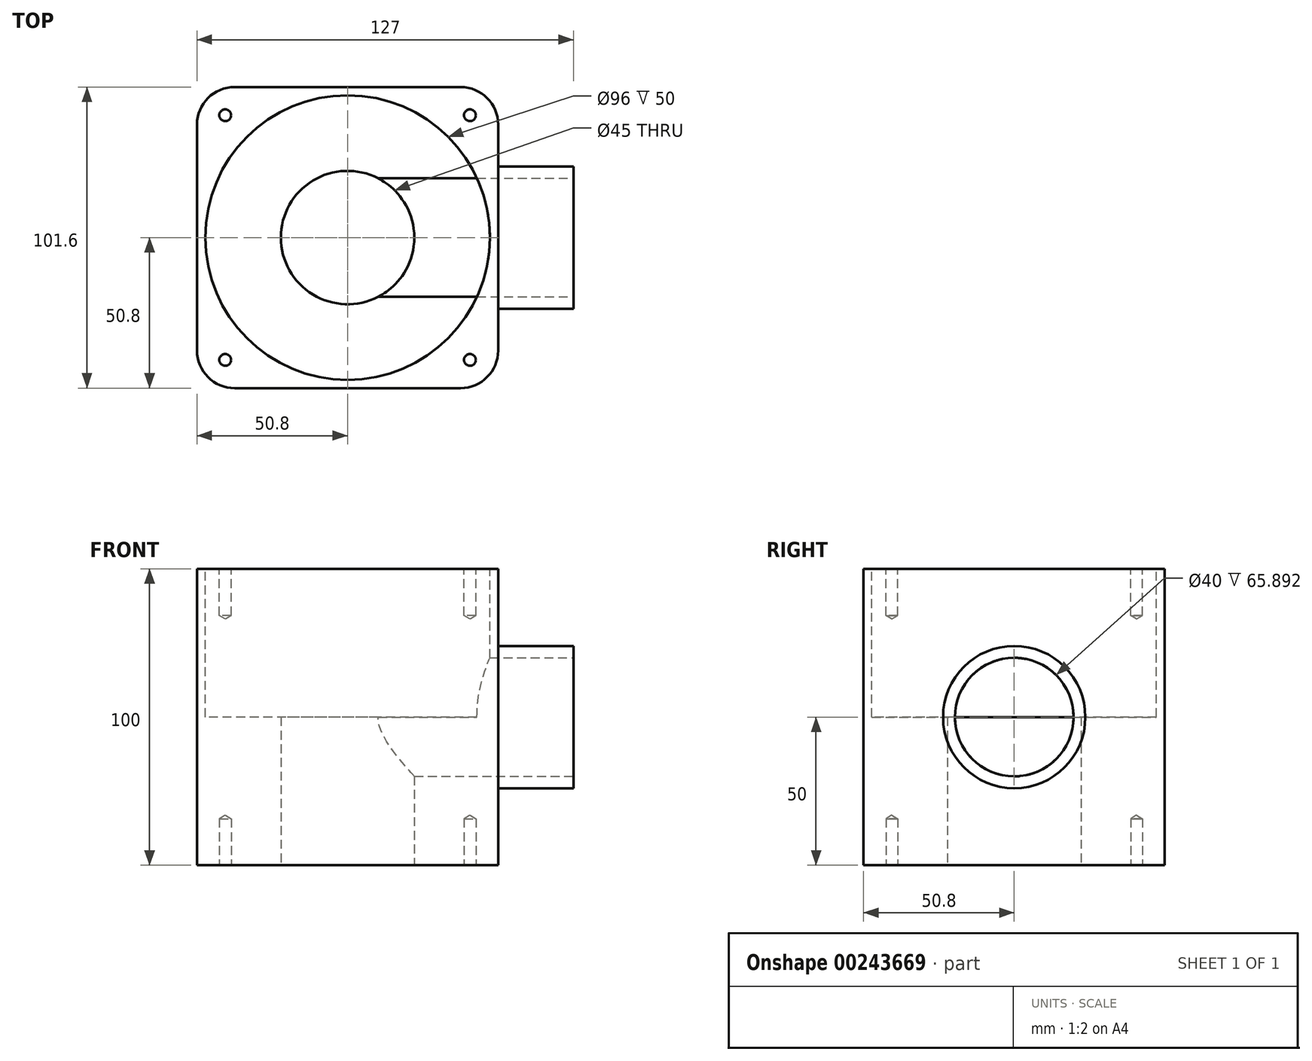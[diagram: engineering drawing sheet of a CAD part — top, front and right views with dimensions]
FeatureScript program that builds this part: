
annotation { "Feature Type Name" : "Feature", "Feature Type Description" : "" }
export const myFeature = defineFeature(function(context is Context, id is Id, definition is map)
    precondition{}
    {
        {
            var Q0;
            Q0=qCreatedBy(makeId("Top.planeOp"),FACE);
            var sketch = newSketch(context, id + "F0", { "sketchPlane" : qUnion([Q0])});
            skLineSegment(sketch, "E0.bottom", {"start": v(-50.8, -50.8) * mm, "end": v(50.8, -50.8) * mm});
            skLineSegment(sketch, "E0.top", {"start": v(-50.8, 50.8) * mm, "end": v(50.8, 50.8) * mm});
            skLineSegment(sketch, "E0.left", {"start": v(-50.8, -50.8) * mm, "end": v(-50.8, 50.8) * mm});
            skLineSegment(sketch, "E0.right", {"start": v(50.8, -50.8) * mm, "end": v(50.8, 50.8) * mm});
            skPoint(sketch, "E0.middle", {"position": v(0, 0) * mm});
            skCircle(sketch, "E1", {"center": v(0, 0) * mm, "radius": 48 * mm});
            skSolve(sketch);
        }
        {
            var Q0;
            Q0 = qSketchRegion(id + "F0", true);
            var Q1;
            Q1=makeQuery(id+"F0.imprint","IMPRINT",FACE,{"disambiguationData":[TD([[makeQuery(id+"F0.imprint","IMPRINT",EDGE,{"derivedFrom":sQuery(id+"F0.wireOp",EDGE,"E1")}),1.0]])]});
            extrude(context, id + "F1", {"entities" : qUnion([Q0, Q1]), "endBound" : BoundingType.SYMMETRIC, "depth" : 100 * mm});
        }
        {
            var Q0;
            Q0=makeQuery(id+"F1.opExtrude","SWEPT_FACE",FACE,{"disambiguationData":[OSD([sQuery(id+"F0.wireOp",EDGE,"E0.right")])]});
            var sketch = newSketch(context, id + "F2", { "sketchPlane" : qUnion([Q0])});
            skCircle(sketch, "E2", {"center": v(0, 0) * mm, "radius": 20 * mm});
            skSolve(sketch);
        }
        {
            var Q0;
            Q0 = qSketchRegion(id + "F2", true);
            extrude(context, id + "F3", {"entities" : qUnion([Q0]), "operationType" : NewBodyOperationType.REMOVE, "oppositeDirection" : true, "depth" : 50.8 * mm});
        }
        {
            var Q0;
            Q0=makeQuery(id+"F1.opExtrude","CAP_FACE",FACE,{"disambiguationData":[OSD([sQuery(id+"F0.wireOp",EDGE,"E0.bottom"),sQuery(id+"F0.wireOp",EDGE,"E0.top"),sQuery(id+"F0.wireOp",EDGE,"E0.left"),sQuery(id+"F0.wireOp",EDGE,"E0.right")])],"isStart":false});
            var sketch = newSketch(context, id + "F4", { "sketchPlane" : qUnion([Q0])});
            skCircle(sketch, "E3", {"center": v(0, 0) * mm, "radius": 48 * mm});
            skSolve(sketch);
        }
        {
            var Q0;
            Q0=makeQuery(id+"F4.imprint","IMPRINT",FACE,{"disambiguationData":[TD([[makeQuery(id+"F4.imprint","IMPRINT",EDGE,{"derivedFrom":sQuery(id+"F4.wireOp",EDGE,"E3")}),1.0]])]});
            extrude(context, id + "F5", {"entities" : qUnion([Q0]), "operationType" : NewBodyOperationType.REMOVE, "oppositeDirection" : true, "depth" : 50 * mm});
        }
        {
            var Q0;
            Q0=makeQuery(id+"F1.opExtrude","CAP_FACE",FACE,{"disambiguationData":[OSD([sQuery(id+"F0.wireOp",EDGE,"E0.bottom"),sQuery(id+"F0.wireOp",EDGE,"E0.top"),sQuery(id+"F0.wireOp",EDGE,"E0.left"),sQuery(id+"F0.wireOp",EDGE,"E0.right")])],"isStart":true});
            var sketch = newSketch(context, id + "F6", { "sketchPlane" : qUnion([Q0])});
            skCircle(sketch, "E4", {"center": v(0, 0) * mm, "radius": 22.5 * mm});
            skSolve(sketch);
        }
        {
            var Q0;
            Q0 = qSketchRegion(id + "F6", true);
            extrude(context, id + "F7", {"entities" : qUnion([Q0]), "operationType" : NewBodyOperationType.REMOVE, "endBound" : BoundingType.THROUGH_ALL, "oppositeDirection" : true, "depth" : 25.4 * mm});
        }
        {
            var Q0;
            Q0=makeQuery(id+"F1.opExtrude","SWEPT_FACE",FACE,{"disambiguationData":[OSD([sQuery(id+"F0.wireOp",EDGE,"E0.right")])]});
            var sketch = newSketch(context, id + "F8", { "sketchPlane" : qUnion([Q0])});
            skCircle(sketch, "E5", {"center": v(0, 0) * mm, "radius": 24 * mm});
            skCircle(sketch, "E6.0", {"center": v(0, 0) * mm, "radius": 20 * mm});
            skSolve(sketch);
        }
        {
            var Q0;
            Q0 = qSketchRegion(id + "F8", true);
            extrude(context, id + "F9", {"entities" : qUnion([Q0]), "operationType" : NewBodyOperationType.ADD, "depth" : 25.4 * mm});
        }
        {
            var Q0;
            Q0=makeQuery(id+"F1.opExtrude","SWEPT_EDGE",EDGE,{"disambiguationData":[OSD([sQuery(id+"F0.wireOp",EDGE,"E0.bottom"),sQuery(id+"F0.wireOp",EDGE,"E0.right")])]});
            var Q1;
            Q1=makeQuery(id+"F1.opExtrude","SWEPT_EDGE",EDGE,{"disambiguationData":[OSD([sQuery(id+"F0.wireOp",EDGE,"E0.bottom"),sQuery(id+"F0.wireOp",EDGE,"E0.left")])]});
            var Q2;
            Q2=makeQuery(id+"F1.opExtrude","SWEPT_EDGE",EDGE,{"disambiguationData":[OSD([sQuery(id+"F0.wireOp",EDGE,"E0.top"),sQuery(id+"F0.wireOp",EDGE,"E0.right")])]});
            var Q3;
            Q3=makeQuery(id+"F1.opExtrude","SWEPT_EDGE",EDGE,{"disambiguationData":[OSD([sQuery(id+"F0.wireOp",EDGE,"E0.top"),sQuery(id+"F0.wireOp",EDGE,"E0.left")])]});
            fillet(context, id + "F10", {"entities" : qUnion([Q0, Q1, Q2, Q3]), "radius" : 12.7 * mm, "tangentPropagation" : true, "allowEdgeOverflow" : false});
        }
        {
            var Q0;
            Q0=makeQuery(id+"F1.opExtrude","CAP_FACE",FACE,{"disambiguationData":[OSD([sQuery(id+"F0.wireOp",EDGE,"E0.bottom"),sQuery(id+"F0.wireOp",EDGE,"E0.top"),sQuery(id+"F0.wireOp",EDGE,"E0.left"),sQuery(id+"F0.wireOp",EDGE,"E0.right")])],"isStart":false});
            var sketch = newSketch(context, id + "F11", { "sketchPlane" : qUnion([Q0])});
            skLineSegment(sketch, "E7.bottom", {"start": v(-41.28, -41.28) * mm, "end": v(41.28, -41.28) * mm, "construction": true});
            skLineSegment(sketch, "E7.top", {"start": v(-41.28, 41.28) * mm, "end": v(41.28, 41.28) * mm, "construction": true});
            skLineSegment(sketch, "E7.left", {"start": v(-41.28, -41.28) * mm, "end": v(-41.28, 41.28) * mm, "construction": true});
            skLineSegment(sketch, "E7.right", {"start": v(41.28, -41.27) * mm, "end": v(41.28, 41.28) * mm, "construction": true});
            skPoint(sketch, "E7.middle", {"position": v(0, 0) * mm});
            skSolve(sketch);
        }
        {
            var Q0;
            Q0=sQuery(id+"F11.wireOp",VERTEX,"E7.top.start");
            var Q1;
            Q1=sQuery(id+"F11.wireOp",VERTEX,"E7.top.end");
            var Q2;
            Q2=sQuery(id+"F11.wireOp",VERTEX,"E7.bottom.end");
            var Q3;
            Q3=sQuery(id+"F11.wireOp",VERTEX,"E7.bottom.start");
            var Q4;
            Q4=makeQuery(id+"F1.opExtrude","SWEPT_BODY",BODY,{"disambiguationData":[OSD([sQuery(id+"F0.wireOp",EDGE,"E0.bottom"),sQuery(id+"F0.wireOp",EDGE,"E0.top"),sQuery(id+"F0.wireOp",EDGE,"E0.left"),sQuery(id+"F0.wireOp",EDGE,"E0.right")])]});
            hole(context, id + "F12", {"style" : HoleStyle.SIMPLE, "endStyle" : HoleEndStyle.BLIND, "standardTappedOrClearance" : lookupTablePath({ "standard" : "ISO", "engagement" : "75%", "pitch" : "1 mm", "size" : "M5", "type" : "Tapped" }), "standardBlindInLast" : lookupTablePath({ "standard" : "ISO", "engagement" : "75%", "pitch" : "1 mm", "size" : "M5", "type" : "Tapped" }), "holeDiameter" : 4 * mm, "showTappedDepth" : true, "holeDepth" : 15.7 * mm, "tappedDepth" : 12.7 * mm, "tapClearance" : 3, "locations" : qUnion([Q0, Q1, Q2, Q3]), "scope" : qUnion([Q4])});
        }
        {
            var Q0;
            Q0=makeQuery(id+"F1.opExtrude","CAP_FACE",FACE,{"disambiguationData":[OSD([sQuery(id+"F0.wireOp",EDGE,"E0.bottom"),sQuery(id+"F0.wireOp",EDGE,"E0.top"),sQuery(id+"F0.wireOp",EDGE,"E0.left"),sQuery(id+"F0.wireOp",EDGE,"E0.right")])],"isStart":true});
            var sketch = newSketch(context, id + "F13", { "sketchPlane" : qUnion([Q0])});
            skLineSegment(sketch, "E8.bottom", {"start": v(-41.28, -41.28) * mm, "end": v(41.28, -41.28) * mm, "construction": true});
            skLineSegment(sketch, "E8.top", {"start": v(-41.28, 41.28) * mm, "end": v(41.28, 41.28) * mm, "construction": true});
            skLineSegment(sketch, "E8.left", {"start": v(-41.28, -41.28) * mm, "end": v(-41.28, 41.28) * mm, "construction": true});
            skLineSegment(sketch, "E8.right", {"start": v(41.28, -41.28) * mm, "end": v(41.28, 41.27) * mm, "construction": true});
            skPoint(sketch, "E8.middle", {"position": v(0, 0) * mm});
            skSolve(sketch);
        }
        {
            var Q0;
            Q0=sQuery(id+"F13.wireOp",VERTEX,"E8.left.end");
            var Q1;
            Q1=sQuery(id+"F13.wireOp",VERTEX,"E8.right.end");
            var Q2;
            Q2=sQuery(id+"F13.wireOp",VERTEX,"E8.left.start");
            var Q3;
            Q3=sQuery(id+"F13.wireOp",VERTEX,"E8.right.start");
            var Q4;
            Q4=makeQuery(id+"F1.opExtrude","SWEPT_BODY",BODY,{"disambiguationData":[OSD([sQuery(id+"F0.wireOp",EDGE,"E0.bottom"),sQuery(id+"F0.wireOp",EDGE,"E0.top"),sQuery(id+"F0.wireOp",EDGE,"E0.left"),sQuery(id+"F0.wireOp",EDGE,"E0.right")])]});
            hole(context, id + "F14", {"style" : HoleStyle.SIMPLE, "endStyle" : HoleEndStyle.BLIND, "standardTappedOrClearance" : lookupTablePath({ "standard" : "ISO", "engagement" : "75%", "pitch" : "1 mm", "size" : "M5", "type" : "Tapped" }), "standardBlindInLast" : lookupTablePath({ "standard" : "ISO", "engagement" : "75%", "pitch" : "1 mm", "size" : "M5", "type" : "Tapped" }), "holeDiameter" : 4 * mm, "showTappedDepth" : true, "holeDepth" : 15.7 * mm, "tappedDepth" : 12.7 * mm, "tapClearance" : 3, "locations" : qUnion([Q0, Q1, Q2, Q3]), "scope" : qUnion([Q4])});
        }
    });
